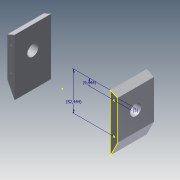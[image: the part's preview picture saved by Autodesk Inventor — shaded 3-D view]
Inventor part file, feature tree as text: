
AUTODESK INVENTOR PART (.ipt)
format: ipt  version: 2013 (Build 170138000, 138)  size: 118,272 bytes
history: native  units: mm
features: sketch x9, hole x4, extrude x1
ambient origin geometry x8: Origin, YZ Plane, XZ Plane, XY Plane, X Axis, Y Axis, Z Axis, Center Point
bodies: Solid1 (feature_tree)
feature tree (14):
  sketch  "Sketch1"  dims[d3=10.0mm d4=53.0mm]
  sketch  "Sketch2"  dims[d8=10.0mm d9=53.0mm]
  sketch  "Sketch3"  dims[d11=50.0mm d12=0.0mm d15=15.0mm]
  extrude  "Extrusion1"  Depth=53.0mm
  hole  "Hole1"  [1 undecoded]
  hole  "Hole2"  [1 undecoded]
  hole  "Hole3"  [1 undecoded]
  sketch  "Sketch7"  dims[d47=2.0mm d48=6.0mm d49=4.0mm d50=2.0mm d51=90.0deg d52=50.0mm d53=0.0mm d54=5.0mm]
  hole  "Hole4"  [1 undecoded]
  sketch  "Sketch9"
  sketch  "Sketch4"  dims[d16=15.0mm d17=6.0mm d18=4.0mm d19=2.0mm d20=90.0deg d21=151.0mm d22=0.0mm]
  sketch  "Sketch5"  dims[d25=2.0mm d26=6.0mm d27=4.0mm d28=2.0mm d29=90.0deg d30=50.0mm d31=0.0mm]
  sketch  "Sketch6"  dims[d34=2.0mm d35=6.0mm d36=4.0mm d37=2.0mm d38=90.0deg d39=50.0mm d40=0.0mm]
  sketch  "Sketch8"  dims[d55=9.444444mm d56=52.444444mm]
note: 4 required parameter values undecoded (feature->parameter linkage not recoverable at this tier; creation-order binding heuristic only, values carry confidence <= 0.55)
